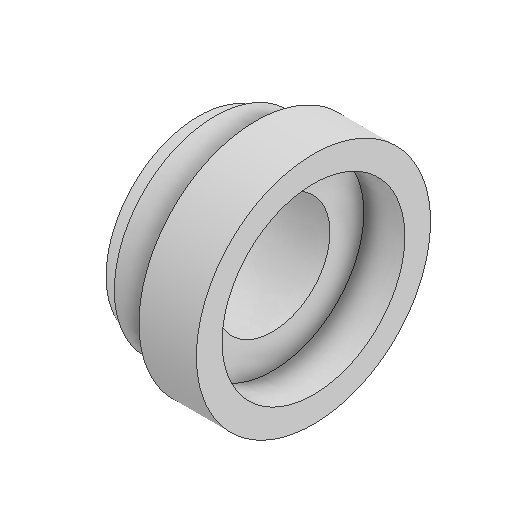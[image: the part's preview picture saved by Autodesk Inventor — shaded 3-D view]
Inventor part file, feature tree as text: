
AUTODESK INVENTOR PART (.ipt)
format: ipt  version: 2025 (Build 290162000, 162)  size: 156,672 bytes
history: native  units: in
note: dims shown in document units (in); Inventor stores cm internally (conversion verified against a paired STEP export)
features: extrude x3, sketch x3, projected_geometry x2, chamfer x1
ambient origin geometry x8: Origin, YZ Plane, XZ Plane, XY Plane, X Axis, Y Axis, Z Axis, Center Point
bodies: Solid1 (feature_tree)
feature tree (9):
  extrude  "Extrusion1"  Depth=1.122in
  extrude  "Extrusion2"  Depth=0.2756in
  extrude  "Extrusion3"  Depth=0.2756in TaperAngle=0.0deg
  chamfer  "Chamfer1"  Distance=0.0787in
  sketch  "Sketch1"  dims[d0=0.876in d1=1.122in]
  sketch  "Sketch2"  dims[d2=0.2756in d3=0.0in d4=0.9646in]
  projected_geometry  "Projected Loop1"
  sketch  "Sketch3"  dims[d5=0.5512in d6=0.2756in d7=0.0in d8=0.0787in d9=0.0in d10=0.0394in d11=0.0787in d12=45.0deg]
  projected_geometry  "Projected Loop2"
